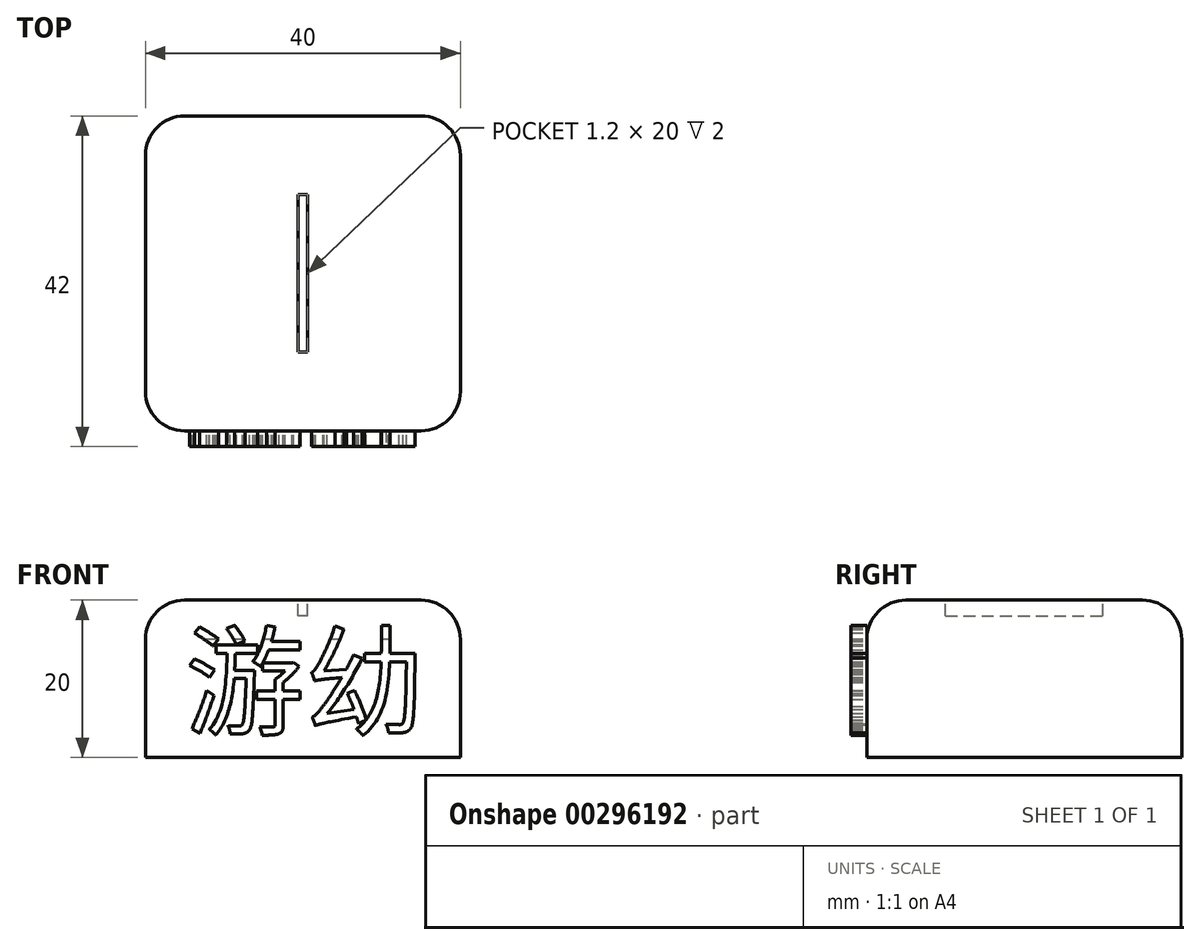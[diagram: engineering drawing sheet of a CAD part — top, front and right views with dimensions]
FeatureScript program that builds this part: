
annotation { "Feature Type Name" : "Feature", "Feature Type Description" : "" }
export const myFeature = defineFeature(function(context is Context, id is Id, definition is map)
    precondition{}
    {
        {
            var Q0;
            Q0=qCreatedBy(makeId("Top.planeOp"),FACE);
            var sketch = newSketch(context, id + "F0", { "sketchPlane" : qUnion([Q0])});
            skLineSegment(sketch, "E0.bottom", {"start": v(20, -20) * mm, "end": v(-20, -20) * mm});
            skLineSegment(sketch, "E0.top", {"start": v(20, 20) * mm, "end": v(-20, 20) * mm});
            skLineSegment(sketch, "E0.left", {"start": v(20, -20) * mm, "end": v(20, 20) * mm});
            skLineSegment(sketch, "E0.right", {"start": v(-20, -20) * mm, "end": v(-20, 20) * mm});
            skPoint(sketch, "E0.middle", {"position": v(0, 0) * mm});
            skLineSegment(sketch, "E1.bottom", {"start": v(0.6, -10) * mm, "end": v(-0.6, -10) * mm});
            skLineSegment(sketch, "E1.top", {"start": v(0.6, 10) * mm, "end": v(-0.6, 10) * mm});
            skLineSegment(sketch, "E1.left", {"start": v(0.6, -10) * mm, "end": v(0.6, 10) * mm});
            skLineSegment(sketch, "E1.right", {"start": v(-0.6, -10) * mm, "end": v(-0.6, 10) * mm});
            skSolve(sketch);
        }
        {
            var Q0;
            Q0=makeQuery(id+"F0.imprint","IMPRINT",FACE,{"disambiguationData":[TD([[makeQuery(id+"F0.imprint","IMPRINT",EDGE,{"derivedFrom":sQuery(id+"F0.wireOp",EDGE,"E0.bottom")}),-1.0]])]});
            var Q1;
            Q1=makeQuery(id+"F0.imprint","IMPRINT",FACE,{"disambiguationData":[TD([[makeQuery(id+"F0.imprint","IMPRINT",EDGE,{"derivedFrom":sQuery(id+"F0.wireOp",EDGE,"E1.bottom")}),-1.0]])]});
            extrude(context, id + "F1", {"entities" : qUnion([Q0, Q1]), "oppositeDirection" : true, "depth" : 20 * mm});
        }
        {
            var Q0;
            Q0=makeQuery(id+"F0.imprint","IMPRINT",FACE,{"disambiguationData":[TD([[makeQuery(id+"F0.imprint","IMPRINT",EDGE,{"derivedFrom":sQuery(id+"F0.wireOp",EDGE,"E1.bottom")}),-1.0]])]});
            extrude(context, id + "F2", {"entities" : qUnion([Q0]), "operationType" : NewBodyOperationType.REMOVE, "oppositeDirection" : true, "depth" : 2 * mm});
        }
        {
            var Q0;
            Q0=makeQuery(id+"F2.boolean.opBoolean","COPY",EDGE,{"derivedFrom":makeQuery(id+"F2.opExtrude","CAP_EDGE",EDGE,{"disambiguationData":[OSD([sQuery(id+"F0.wireOp",EDGE,"E1.left")])],"isStart":true})});
            var Q1;
            Q1=makeQuery(id+"F2.boolean.opBoolean","COPY",EDGE,{"derivedFrom":makeQuery(id+"F2.opExtrude","CAP_EDGE",EDGE,{"disambiguationData":[OSD([sQuery(id+"F0.wireOp",EDGE,"E1.right")])],"isStart":true})});
            var Q2;
            Q2=makeQuery(id+"F1.opExtrude","SWEPT_EDGE",EDGE,{"disambiguationData":[OSD([sQuery(id+"F0.wireOp",EDGE,"E0.bottom"),sQuery(id+"F0.wireOp",EDGE,"E0.left")])]});
            var Q3;
            Q3=makeQuery(id+"F1.opExtrude","SWEPT_EDGE",EDGE,{"disambiguationData":[OSD([sQuery(id+"F0.wireOp",EDGE,"E0.top"),sQuery(id+"F0.wireOp",EDGE,"E0.left")])]});
            var Q4;
            Q4=makeQuery(id+"F1.opExtrude","CAP_EDGE",EDGE,{"disambiguationData":[OSD([sQuery(id+"F0.wireOp",EDGE,"E0.left")])],"isStart":true});
            var Q5;
            Q5=makeQuery(id+"F1.opExtrude","SWEPT_EDGE",EDGE,{"disambiguationData":[OSD([sQuery(id+"F0.wireOp",EDGE,"E0.bottom"),sQuery(id+"F0.wireOp",EDGE,"E0.right")])]});
            var Q6;
            Q6=makeQuery(id+"F1.opExtrude","SWEPT_EDGE",EDGE,{"disambiguationData":[OSD([sQuery(id+"F0.wireOp",EDGE,"E0.top"),sQuery(id+"F0.wireOp",EDGE,"E0.right")])]});
            var Q7;
            Q7=makeQuery(id+"F1.opExtrude","CAP_EDGE",EDGE,{"disambiguationData":[OSD([sQuery(id+"F0.wireOp",EDGE,"E0.top")])],"isStart":true});
            var Q8;
            Q8=makeQuery(id+"F1.opExtrude","CAP_EDGE",EDGE,{"disambiguationData":[OSD([sQuery(id+"F0.wireOp",EDGE,"E0.right")])],"isStart":true});
            var Q9;
            Q9=makeQuery(id+"F1.opExtrude","CAP_EDGE",EDGE,{"disambiguationData":[OSD([sQuery(id+"F0.wireOp",EDGE,"E0.bottom")])],"isStart":true});
            fillet(context, id + "F3", {"entities" : qUnion([Q0, Q1, Q2, Q3, Q4, Q5, Q6, Q7, Q8, Q9]), "radius" : 5 * mm, "tangentPropagation" : true, "allowEdgeOverflow" : false});
        }
        {
            var Q0;
            Q0=makeQuery(id+"F1.opExtrude","SWEPT_FACE",FACE,{"disambiguationData":[OSD([sQuery(id+"F0.wireOp",EDGE,"E0.bottom")])]});
            var sketch = newSketch(context, id + "F4", { "sketchPlane" : qUnion([Q0])});
            skText(sketch, "E2", { "text": "游幼", "fontName": "NotoSansCJKtc-Regular.otf"});
            const initialGuessF4  = {"E2": [-0.015, -0.01599, 1, 0, 0.01099]};
            skSetInitialGuess(sketch, initialGuessF4);
            skSolve(sketch);
        }
        {
            var Q0;
            Q0=qSketchRegion(id+"F4",true);
            extrude(context, id + "F5", {"entities" : qUnion([Q0]), "operationType" : NewBodyOperationType.ADD, "depth" : 2 * mm});
        }
    });
